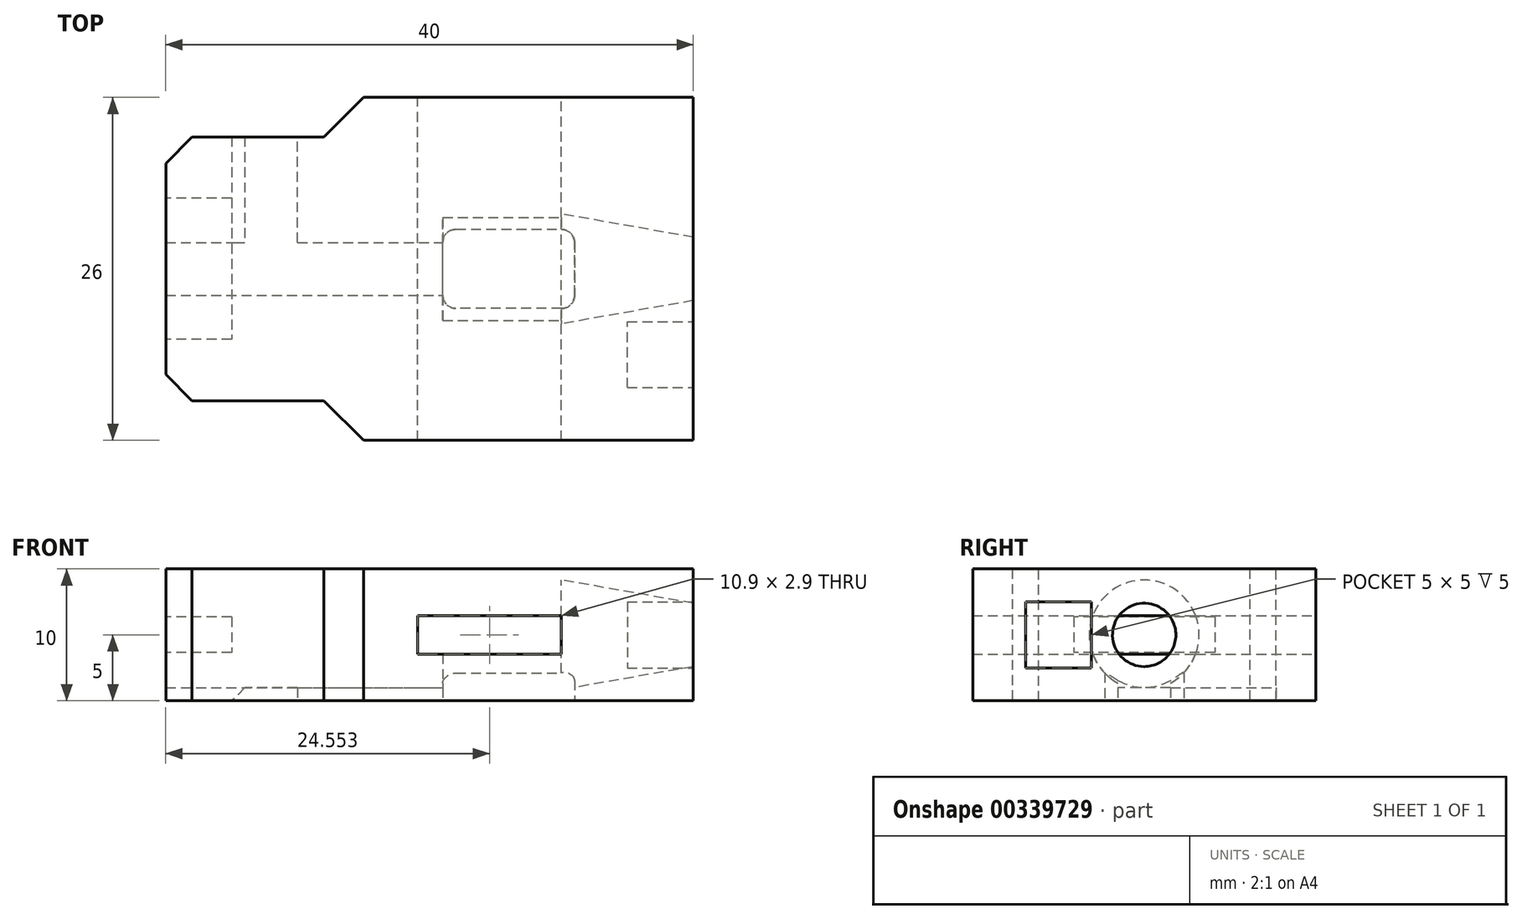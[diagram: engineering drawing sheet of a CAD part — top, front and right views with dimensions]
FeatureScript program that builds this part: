
annotation { "Feature Type Name" : "Feature", "Feature Type Description" : "" }
export const myFeature = defineFeature(function(context is Context, id is Id, definition is map)
    precondition{}
    {
        {
            var Q0;
            Q0=qCreatedBy(makeId("Top.planeOp"),FACE);
            var sketch = newSketch(context, id + "F0", { "sketchPlane" : qUnion([Q0])});
            skPoint(sketch, "E0", {"position": v(-7.73, 0) * mm});
            skLineSegment(sketch, "E1.bottom", {"start": v(-2.73, 10) * mm, "end": v(-12.73, 10) * mm});
            skLineSegment(sketch, "E1.top", {"start": v(-2.73, -10) * mm, "end": v(-12.73, -10) * mm});
            skLineSegment(sketch, "E1.left", {"start": v(-2.73, 10) * mm, "end": v(-2.73, -10) * mm});
            skLineSegment(sketch, "E1.right", {"start": v(-12.73, 10) * mm, "end": v(-12.73, -10) * mm});
            skLineSegment(sketch, "E2", {"start": v(-2.73, 10) * mm, "end": v(-2.73, 13) * mm});
            skLineSegment(sketch, "E3", {"start": v(-2.73, 13) * mm, "end": v(27.27, 13) * mm});
            skLineSegment(sketch, "E4", {"start": v(27.27, 13) * mm, "end": v(27.27, -13) * mm});
            skLineSegment(sketch, "E5", {"start": v(27.27, -13) * mm, "end": v(-2.73, -13) * mm});
            skLineSegment(sketch, "E6", {"start": v(-2.73, -13) * mm, "end": v(-2.73, -10) * mm});
            skSolve(sketch);
        }
        {
            var Q0;
            Q0=makeQuery(id+"F0.imprint","IMPRINT",FACE,{"disambiguationData":[TD([[makeQuery(id+"F0.imprint","IMPRINT",EDGE,{"derivedFrom":sQuery(id+"F0.wireOp",EDGE,"E1.bottom")}),1.0]])]});
            var Q1;
            Q1=makeQuery(id+"F0.imprint","IMPRINT",FACE,{"disambiguationData":[TD([[makeQuery(id+"F0.imprint","IMPRINT",EDGE,{"derivedFrom":sQuery(id+"F0.wireOp",EDGE,"E1.left")}),1.0]])]});
            extrude(context, id + "F1", {"entities" : qUnion([Q0, Q1]), "depth" : 10 * mm});
        }
        {
            var Q0;
            Q0=makeQuery(id+"F1.opExtrude","SWEPT_FACE",FACE,{"disambiguationData":[OSD([sQuery(id+"F0.wireOp",EDGE,"E1.right")])]});
            var sketch = newSketch(context, id + "F2", { "sketchPlane" : qUnion([Q0])});
            skLineSegment(sketch, "E7", {"start": v(-10, 10) * mm, "end": v(10, 0) * mm});
            skLineSegment(sketch, "E8", {"start": v(-10, 0) * mm, "end": v(10, 10) * mm});
            skLineSegment(sketch, "E9.bottom", {"start": v(-5.35, 6.35) * mm, "end": v(5.35, 6.35) * mm});
            skLineSegment(sketch, "E9.top", {"start": v(-5.35, 3.65) * mm, "end": v(5.35, 3.65) * mm});
            skLineSegment(sketch, "E9.left", {"start": v(-5.35, 6.35) * mm, "end": v(-5.35, 3.65) * mm});
            skLineSegment(sketch, "E9.right", {"start": v(5.35, 6.35) * mm, "end": v(5.35, 3.65) * mm});
            skPoint(sketch, "E9.middle", {"position": v(0, 5) * mm});
            skSolve(sketch);
        }
        {
            var Q0;
            {var subQ0=sQuery(id+"F2.wireOp",EDGE,"E9.left");Q0=makeQuery(id+"F2.imprint","IMPRINT",FACE,{"disambiguationData":[TD([[makeQuery(id+"F2.imprint","IMPRINT",EDGE,{"derivedFrom":subQ0}),1.0]])]});}
            var Q1;
            {var subQ0=sQuery(id+"F2.wireOp",EDGE,"E8");var subQ1=sQuery(id+"F2.wireOp",EDGE,"E7");var subQ2=makeQuery(id+"F2.imprint","INTERSECT",VERTEX,{"derivedFrom":[subQ1,subQ0]});Q1=makeQuery(id+"F2.imprint","IMPRINT",FACE,{"disambiguationData":[TD([[makeQuery(id+"F2.imprint","IMPRINT",EDGE,{"disambiguationData":[TD([[subQ2,-1.0]])],"derivedFrom":subQ1}),-1.0]])]});}
            var Q2;
            {var subQ0=sQuery(id+"F2.wireOp",EDGE,"E9.right");Q2=makeQuery(id+"F2.imprint","IMPRINT",FACE,{"disambiguationData":[TD([[makeQuery(id+"F2.imprint","IMPRINT",EDGE,{"derivedFrom":subQ0}),-1.0]])]});}
            var Q3;
            {var subQ0=sQuery(id+"F2.wireOp",EDGE,"E9.bottom");var subQ1=sQuery(id+"F2.wireOp",EDGE,"E7");var subQ2=makeQuery(id+"F2.imprint","INTERSECT",VERTEX,{"derivedFrom":[subQ1,subQ0]});Q3=makeQuery(id+"F2.imprint","IMPRINT",FACE,{"disambiguationData":[TD([[makeQuery(id+"F2.imprint","IMPRINT",EDGE,{"disambiguationData":[TD([[subQ2,-1.0]])],"derivedFrom":subQ1}),1.0]])]});}
            extrude(context, id + "F3", {"entities" : qUnion([Q0, Q1, Q2, Q3]), "operationType" : NewBodyOperationType.REMOVE, "oppositeDirection" : true, "depth" : 5 * mm});
        }
        {
            var Q0;
            Q0=makeQuery(id+"F1.opExtrude","SWEPT_EDGE",EDGE,{"disambiguationData":[OSD([sQuery(id+"F0.wireOp",EDGE,"E2"),sQuery(id+"F0.wireOp",EDGE,"E3")])]});
            var Q1;
            Q1=makeQuery(id+"F1.opExtrude","SWEPT_EDGE",EDGE,{"disambiguationData":[OSD([sQuery(id+"F0.wireOp",EDGE,"E5"),sQuery(id+"F0.wireOp",EDGE,"E6")])]});
            chamfer(context, id + "F4", {"entities" : qUnion([Q0, Q1]), "width" : 5 * mm, "tangentPropagation" : true});
        }
        {
            var Q0;
            Q0=makeQuery(id+"F1.opExtrude","SWEPT_EDGE",EDGE,{"disambiguationData":[OSD([sQuery(id+"F0.wireOp",EDGE,"E1.bottom"),sQuery(id+"F0.wireOp",EDGE,"E1.right")])]});
            var Q1;
            Q1=makeQuery(id+"F1.opExtrude","SWEPT_EDGE",EDGE,{"disambiguationData":[OSD([sQuery(id+"F0.wireOp",EDGE,"E1.top"),sQuery(id+"F0.wireOp",EDGE,"E1.right")])]});
            chamfer(context, id + "F5", {"entities" : qUnion([Q0, Q1]), "width" : 2 * mm, "tangentPropagation" : true});
        }
        {
            var Q0;
            Q0=makeQuery(id+"F1.opExtrude","SWEPT_FACE",FACE,{"disambiguationData":[OSD([sQuery(id+"F0.wireOp",EDGE,"E3")])]});
            var sketch = newSketch(context, id + "F6", { "sketchPlane" : qUnion([Q0])});
            skLineSegment(sketch, "E10", {"start": v(-27.27, 10) * mm, "end": v(-2.27, 0) * mm});
            skLineSegment(sketch, "E11", {"start": v(-2.27, 0) * mm, "end": v(-2.27, 10) * mm});
            skLineSegment(sketch, "E12", {"start": v(-2.27, 10) * mm, "end": v(-27.27, 0) * mm});
            skLineSegment(sketch, "E13", {"start": v(-14.77, 5) * mm, "end": v(-27.27, 5) * mm});
            skLineSegment(sketch, "E14", {"start": v(-14.77, 5) * mm, "end": v(-2.27, 5) * mm});
            skPoint(sketch, "E15", {"position": v(-17.27, 5) * mm});
            skLineSegment(sketch, "E16", {"start": v(-17.27, 5) * mm, "end": v(-17.27, 6.45) * mm});
            skLineSegment(sketch, "E17", {"start": v(-17.27, 6.45) * mm, "end": v(-6.37, 6.45) * mm});
            skLineSegment(sketch, "E18", {"start": v(-6.37, 6.45) * mm, "end": v(-6.37, 5) * mm});
            skLineSegment(sketch, "E19.MirrorCS", {"start": v(-17.27, 3.55) * mm, "end": v(-6.37, 3.55) * mm});
            skLineSegment(sketch, "E20.MirrorCS", {"start": v(-17.27, 5) * mm, "end": v(-17.27, 3.55) * mm});
            skLineSegment(sketch, "E21.MirrorCS", {"start": v(-6.37, 3.55) * mm, "end": v(-6.37, 5) * mm});
            skSolve(sketch);
        }
        {
            var Q0;
            {var subQ5=sQuery(id+"F6.wireOp",EDGE,"E16");Q0=makeQuery(id+"F6.imprint","IMPRINT",FACE,{"disambiguationData":[TD([[makeQuery(id+"F6.imprint","IMPRINT",EDGE,{"derivedFrom":subQ5}),-1.0]])]});}
            var Q1;
            {var subQ3=sQuery(id+"F6.wireOp",EDGE,"E17");var subQ5=sQuery(id+"F6.wireOp",EDGE,"E18");var subQ6=makeQuery(id+"F6.imprint","INTERSECT",VERTEX,{"derivedFrom":[subQ3,subQ5]});Q1=makeQuery(id+"F6.imprint","IMPRINT",FACE,{"disambiguationData":[TD([[makeQuery(id+"F6.imprint","IMPRINT",EDGE,{"disambiguationData":[TD([[subQ6,1.0]])],"derivedFrom":subQ3}),-1.0]])]});}
            var Q2;
            {var subQ5=sQuery(id+"F6.wireOp",EDGE,"E20.MirrorCS");Q2=makeQuery(id+"F6.imprint","IMPRINT",FACE,{"disambiguationData":[TD([[makeQuery(id+"F6.imprint","IMPRINT",EDGE,{"derivedFrom":subQ5}),1.0]])]});}
            var Q3;
            {var subQ3=sQuery(id+"F6.wireOp",EDGE,"E21.MirrorCS");var subQ5=sQuery(id+"F6.wireOp",EDGE,"E19.MirrorCS");var subQ6=makeQuery(id+"F6.imprint","INTERSECT",VERTEX,{"derivedFrom":[subQ5,subQ3]});Q3=makeQuery(id+"F6.imprint","IMPRINT",FACE,{"disambiguationData":[TD([[makeQuery(id+"F6.imprint","IMPRINT",EDGE,{"disambiguationData":[TD([[subQ6,1.0]])],"derivedFrom":subQ5}),1.0]])]});}
            var Q4;
            {var subQ1=sQuery(id+"F6.wireOp",EDGE,"E12");var subQ3=sQuery(id+"F6.wireOp",EDGE,"E18");var subQ4=makeQuery(id+"F6.imprint","INTERSECT",VERTEX,{"derivedFrom":[subQ1,subQ3]});Q4=makeQuery(id+"F6.imprint","IMPRINT",FACE,{"disambiguationData":[TD([[makeQuery(id+"F6.imprint","IMPRINT",EDGE,{"disambiguationData":[TD([[subQ4,-1.0]])],"derivedFrom":subQ3}),-1.0]])]});}
            var Q5;
            {var subQ1=sQuery(id+"F6.wireOp",EDGE,"E10");var subQ3=sQuery(id+"F6.wireOp",EDGE,"E21.MirrorCS");var subQ4=makeQuery(id+"F6.imprint","INTERSECT",VERTEX,{"derivedFrom":[subQ1,subQ3]});Q5=makeQuery(id+"F6.imprint","IMPRINT",FACE,{"disambiguationData":[TD([[makeQuery(id+"F6.imprint","IMPRINT",EDGE,{"disambiguationData":[TD([[subQ4,-1.0]])],"derivedFrom":subQ3}),1.0]])]});}
            var Q6;
            {var subQ1=sQuery(id+"F6.wireOp",EDGE,"E10");var subQ3=sQuery(id+"F6.wireOp",EDGE,"E19.MirrorCS");var subQ4=makeQuery(id+"F6.imprint","INTERSECT",VERTEX,{"derivedFrom":[subQ1,subQ3]});Q6=makeQuery(id+"F6.imprint","IMPRINT",FACE,{"disambiguationData":[TD([[makeQuery(id+"F6.imprint","IMPRINT",EDGE,{"disambiguationData":[TD([[subQ4,1.0]])],"derivedFrom":subQ3}),1.0]])]});}
            var Q7;
            {var subQ1=sQuery(id+"F6.wireOp",EDGE,"E10");var subQ3=sQuery(id+"F6.wireOp",EDGE,"E17");var subQ4=makeQuery(id+"F6.imprint","INTERSECT",VERTEX,{"derivedFrom":[subQ1,subQ3]});Q7=makeQuery(id+"F6.imprint","IMPRINT",FACE,{"disambiguationData":[TD([[makeQuery(id+"F6.imprint","IMPRINT",EDGE,{"disambiguationData":[TD([[subQ4,-1.0]])],"derivedFrom":subQ3}),-1.0]])]});}
            var Q8;
            Q8=makeQuery(id+"F1.opExtrude","SWEPT_FACE",FACE,{"disambiguationData":[OSD([sQuery(id+"F0.wireOp",EDGE,"E5")])]});
            extrude(context, id + "F7", {"entities" : qUnion([Q0, Q1, Q2, Q3, Q4, Q5, Q6, Q7]), "operationType" : NewBodyOperationType.REMOVE, "endBound" : BoundingType.UP_TO_SURFACE, "oppositeDirection" : true, "endBoundEntityFace" : qUnion([Q8]), "depth" : 25 * mm});
        }
        {
            var Q0;
            Q0=makeQuery(id+"F1.opExtrude","SWEPT_FACE",FACE,{"disambiguationData":[OSD([sQuery(id+"F0.wireOp",EDGE,"E4")])]});
            var sketch = newSketch(context, id + "F8", { "sketchPlane" : qUnion([Q0])});
            skLineSegment(sketch, "E22", {"start": v(13, 0) * mm, "end": v(-13, 10) * mm});
            skLineSegment(sketch, "E23", {"start": v(13, 10) * mm, "end": v(-13, 0) * mm});
            skPoint(sketch, "E24", {"position": v(0, 5) * mm});
            skCircle(sketch, "E25", {"center": v(0, 5) * mm, "radius": 2.4 * mm});
            skLineSegment(sketch, "E26", {"start": v(0, 5) * mm, "end": v(-13, 5) * mm});
            skPoint(sketch, "E27", {"position": v(-6.5, 5) * mm});
            skLineSegment(sketch, "E28.bottom", {"start": v(-9, 7.5) * mm, "end": v(-4, 7.5) * mm});
            skLineSegment(sketch, "E28.top", {"start": v(-9, 2.5) * mm, "end": v(-4, 2.5) * mm});
            skLineSegment(sketch, "E28.left", {"start": v(-9, 7.5) * mm, "end": v(-9, 2.5) * mm});
            skLineSegment(sketch, "E28.right", {"start": v(-4, 7.5) * mm, "end": v(-4, 2.5) * mm});
            skSolve(sketch);
        }
        {
            var Q0;
            {var subQ0=sQuery(id+"F8.wireOp",EDGE,"E23");var subQ1=sQuery(id+"F8.wireOp",EDGE,"E22");var subQ2=makeQuery(id+"F8.imprint","INTERSECT",VERTEX,{"derivedFrom":[subQ1,subQ0]});Q0=makeQuery(id+"F8.imprint","IMPRINT",FACE,{"disambiguationData":[TD([[makeQuery(id+"F8.imprint","IMPRINT",EDGE,{"disambiguationData":[TD([[subQ2,-1.0]])],"derivedFrom":subQ1}),1.0]])]});}
            var Q1;
            {var subQ0=sQuery(id+"F8.wireOp",EDGE,"E23");var subQ1=sQuery(id+"F8.wireOp",EDGE,"E22");var subQ2=makeQuery(id+"F8.imprint","INTERSECT",VERTEX,{"derivedFrom":[subQ1,subQ0]});Q1=makeQuery(id+"F8.imprint","IMPRINT",FACE,{"disambiguationData":[TD([[makeQuery(id+"F8.imprint","IMPRINT",EDGE,{"disambiguationData":[TD([[subQ2,-1.0]])],"derivedFrom":subQ1}),-1.0]])]});}
            var Q2;
            {var subQ0=sQuery(id+"F8.wireOp",EDGE,"E25");var subQ1=sQuery(id+"F8.wireOp",EDGE,"E22");var subQ2=makeQuery(id+"F8.imprint","INTERSECT",VERTEX,{"disambiguationData":[OD(0.0)],"derivedFrom":[subQ1,subQ0]});Q2=makeQuery(id+"F8.imprint","IMPRINT",FACE,{"disambiguationData":[TD([[makeQuery(id+"F8.imprint","IMPRINT",EDGE,{"disambiguationData":[TD([[subQ2,-1.0]])],"derivedFrom":subQ1}),-1.0]])]});}
            var Q3;
            {var subQ0=sQuery(id+"F8.wireOp",EDGE,"E25");var subQ1=sQuery(id+"F8.wireOp",EDGE,"E22");var subQ2=makeQuery(id+"F8.imprint","INTERSECT",VERTEX,{"disambiguationData":[OD(0.0)],"derivedFrom":[subQ1,subQ0]});Q3=makeQuery(id+"F8.imprint","IMPRINT",FACE,{"disambiguationData":[TD([[makeQuery(id+"F8.imprint","IMPRINT",EDGE,{"disambiguationData":[TD([[subQ2,-1.0]])],"derivedFrom":subQ1}),1.0]])]});}
            var Q4;
            {var subQ1=sQuery(id+"F8.wireOp",EDGE,"E23");var subQ3=sQuery(id+"F8.wireOp",EDGE,"E25");var subQ4=makeQuery(id+"F8.imprint","INTERSECT",VERTEX,{"disambiguationData":[OD(1.0)],"derivedFrom":[subQ1,subQ3]});Q4=makeQuery(id+"F8.imprint","IMPRINT",FACE,{"disambiguationData":[TD([[makeQuery(id+"F8.imprint","IMPRINT",EDGE,{"disambiguationData":[TD([[subQ4,1.0]])],"derivedFrom":subQ3}),1.0]])]});}
            var Q5;
            Q5=makeQuery(id+"F7.boolean.opBoolean","COPY",FACE,{"derivedFrom":makeQuery(id+"F7.opExtrude","SWEPT_FACE",FACE,{"disambiguationData":[OSD([sQuery(id+"F6.wireOp",EDGE,"E16"),sQuery(id+"F6.wireOp",EDGE,"E20.MirrorCS")])]})});
            extrude(context, id + "F9", {"entities" : qUnion([Q0, Q1, Q2, Q3, Q4]), "operationType" : NewBodyOperationType.REMOVE, "endBound" : BoundingType.UP_TO_SURFACE, "oppositeDirection" : true, "endBoundEntityFace" : qUnion([Q5]), "depth" : 25 * mm, "hasDraft" : true, "draftAngle" : 10 * degree});
        }
        {
            var Q0;
            Q0=makeQuery(id+"F1.opExtrude","CAP_FACE",FACE,{"disambiguationData":[OSD([sQuery(id+"F0.wireOp",EDGE,"E1.bottom"),sQuery(id+"F0.wireOp",EDGE,"E1.top"),sQuery(id+"F0.wireOp",EDGE,"E1.right"),sQuery(id+"F0.wireOp",EDGE,"E2"),sQuery(id+"F0.wireOp",EDGE,"E3"),sQuery(id+"F0.wireOp",EDGE,"E4"),sQuery(id+"F0.wireOp",EDGE,"E5"),sQuery(id+"F0.wireOp",EDGE,"E6")])],"isStart":true});
            var sketch = newSketch(context, id + "F10", { "sketchPlane" : qUnion([Q0])});
            skPoint(sketch, "E29", {"position": v(17.27, 0) * mm});
            skLineSegment(sketch, "E30.bottom", {"start": v(18.27, 3) * mm, "end": v(16.27, 3) * mm});
            skLineSegment(sketch, "E30.top", {"start": v(18.27, -3) * mm, "end": v(16.27, -3) * mm});
            skLineSegment(sketch, "E30.left", {"start": v(18.27, 3) * mm, "end": v(18.27, -3) * mm});
            skLineSegment(sketch, "E31", {"start": v(18.27, 3) * mm, "end": v(8.27, 3) * mm});
            skLineSegment(sketch, "E32", {"start": v(8.27, 3) * mm, "end": v(8.27, -3) * mm});
            skLineSegment(sketch, "E33", {"start": v(8.27, -3) * mm, "end": v(18.27, -3) * mm});
            skSolve(sketch);
        }
        {
            var Q0;
            Q0 = qSketchRegion(id + "F10", true);
            extrude(context, id + "F11", {"entities" : qUnion([Q0]), "operationType" : NewBodyOperationType.REMOVE, "oppositeDirection" : true, "depth" : 5 * mm});
        }
        {
            var Q0;
            {var subQ1=makeQuery(id+"F7.boolean.opBoolean","COPY",FACE,{"derivedFrom":makeQuery(id+"F7.opExtrude","SWEPT_FACE",FACE,{"disambiguationData":[OSD([sQuery(id+"F6.wireOp",EDGE,"E19.MirrorCS")])]})});var subQ2=sQuery(id+"F8.wireOp",EDGE,"E25");Q0=makeQuery(id+"F11.boolean.opBoolean","SPLIT",FACE,{"disambiguationData":[TD([makeQuery(id+"F11.opExtrude","SWEPT_FACE",FACE,{"disambiguationData":[OSD([sQuery(id+"F10.wireOp",EDGE,"E33")])]})])],"derivedFrom":makeQuery(id+"F9.boolean.opBoolean","COPY",FACE,{"disambiguationData":[TD([subQ1])],"derivedFrom":makeQuery(id+"F9.opExtrude","CAP_FACE",FACE,{"disambiguationData":[OSD([subQ2])],"isStart":false})})});}
            var Q1;
            {var subQ1=makeQuery(id+"F7.boolean.opBoolean","COPY",FACE,{"derivedFrom":makeQuery(id+"F7.opExtrude","SWEPT_FACE",FACE,{"disambiguationData":[OSD([sQuery(id+"F6.wireOp",EDGE,"E19.MirrorCS")])]})});var subQ2=sQuery(id+"F8.wireOp",EDGE,"E25");Q1=makeQuery(id+"F11.boolean.opBoolean","SPLIT",FACE,{"disambiguationData":[TD([makeQuery(id+"F11.opExtrude","SWEPT_FACE",FACE,{"disambiguationData":[OSD([sQuery(id+"F10.wireOp",EDGE,"E31")])]})])],"derivedFrom":makeQuery(id+"F9.boolean.opBoolean","COPY",FACE,{"disambiguationData":[TD([subQ1])],"derivedFrom":makeQuery(id+"F9.opExtrude","CAP_FACE",FACE,{"disambiguationData":[OSD([subQ2])],"isStart":false})})});}
            var Q2;
            Q2=makeQuery(id+"F11.boolean.opBoolean","COPY",FACE,{"derivedFrom":makeQuery(id+"F11.opExtrude","SWEPT_FACE",FACE,{"disambiguationData":[OSD([sQuery(id+"F10.wireOp",EDGE,"E32")])]})});
            extrude(context, id + "F12", {"entities" : qUnion([Q0, Q1]), "operationType" : NewBodyOperationType.REMOVE, "endBound" : BoundingType.UP_TO_SURFACE, "oppositeDirection" : true, "endBoundEntityFace" : qUnion([Q2]), "depth" : 4.47 * mm});
        }
        {
            var Q0;
            Q0=makeQuery(id+"F11.boolean.opBoolean","COPY",EDGE,{"derivedFrom":makeQuery(id+"F11.opExtrude","SWEPT_EDGE",EDGE,{"disambiguationData":[OSD([sQuery(id+"F10.wireOp",EDGE,"E30.left"),sQuery(id+"F10.wireOp",EDGE,"E31")])]})});
            var Q1;
            Q1=makeQuery(id+"F11.boolean.opBoolean","COPY",EDGE,{"derivedFrom":makeQuery(id+"F11.opExtrude","SWEPT_EDGE",EDGE,{"disambiguationData":[OSD([sQuery(id+"F10.wireOp",EDGE,"E31"),sQuery(id+"F10.wireOp",EDGE,"E32")])]})});
            var Q2;
            Q2=makeQuery(id+"F11.boolean.opBoolean","COPY",EDGE,{"derivedFrom":makeQuery(id+"F11.opExtrude","SWEPT_EDGE",EDGE,{"disambiguationData":[OSD([sQuery(id+"F10.wireOp",EDGE,"E32"),sQuery(id+"F10.wireOp",EDGE,"E33")])]})});
            var Q3;
            Q3=makeQuery(id+"F11.boolean.opBoolean","COPY",EDGE,{"derivedFrom":makeQuery(id+"F11.opExtrude","SWEPT_EDGE",EDGE,{"disambiguationData":[OSD([sQuery(id+"F10.wireOp",EDGE,"E30.left"),sQuery(id+"F10.wireOp",EDGE,"E33")])]})});
            fillet(context, id + "F13", {"entities" : qUnion([Q0, Q1, Q2, Q3]), "radius" : 1 * mm, "tangentPropagation" : true, "allowEdgeOverflow" : false});
        }
        {
            var Q0;
            Q0=makeQuery(id+"F1.opExtrude","CAP_FACE",FACE,{"disambiguationData":[OSD([sQuery(id+"F0.wireOp",EDGE,"E1.bottom"),sQuery(id+"F0.wireOp",EDGE,"E1.top"),sQuery(id+"F0.wireOp",EDGE,"E1.right"),sQuery(id+"F0.wireOp",EDGE,"E2"),sQuery(id+"F0.wireOp",EDGE,"E3"),sQuery(id+"F0.wireOp",EDGE,"E4"),sQuery(id+"F0.wireOp",EDGE,"E5"),sQuery(id+"F0.wireOp",EDGE,"E6")])],"isStart":true});
            var sketch = newSketch(context, id + "F14", { "sketchPlane" : qUnion([Q0])});
            skLineSegment(sketch, "E34.bottom", {"start": v(-12.73, 2) * mm, "end": v(18.27, 2) * mm});
            skLineSegment(sketch, "E34.top", {"start": v(-12.73, -2) * mm, "end": v(18.27, -2) * mm});
            skLineSegment(sketch, "E34.left", {"start": v(-12.73, 2) * mm, "end": v(-12.73, -2) * mm});
            skLineSegment(sketch, "E34.right", {"start": v(18.27, 2) * mm, "end": v(18.27, -2) * mm});
            skLineSegment(sketch, "E35.bottom", {"start": v(-12.73, -2) * mm, "end": v(-2.73, -2) * mm});
            skLineSegment(sketch, "E35.top", {"start": v(-6.73, -10) * mm, "end": v(-2.73, -10) * mm});
            skLineSegment(sketch, "E35.right", {"start": v(-2.73, -2) * mm, "end": v(-2.73, -10) * mm});
            skLineSegment(sketch, "E36", {"start": v(-6.73, -10) * mm, "end": v(-6.73, -2) * mm});
            skSolve(sketch);
        }
        {
            var Q0;
            {var subQ1=sQuery(id+"F14.wireOp",EDGE,"E34.left");Q0=makeQuery(id+"F14.imprint","IMPRINT",FACE,{"disambiguationData":[TD([[makeQuery(id+"F14.imprint","IMPRINT",EDGE,{"derivedFrom":subQ1}),-1.0]])]});}
            var Q1;
            Q1=makeQuery(id+"F14.imprint","IMPRINT",FACE,{"disambiguationData":[TD([[makeQuery(id+"F14.imprint","IMPRINT",EDGE,{"derivedFrom":sQuery(id+"F14.wireOp",EDGE,"E35.top")}),-1.0]])]});
            extrude(context, id + "F15", {"entities" : qUnion([Q0, Q1]), "operationType" : NewBodyOperationType.REMOVE, "oppositeDirection" : true, "depth" : 1 * mm});
        }
        {
            var Q0;
            Q0=makeQuery(id+"F15.boolean.opBoolean","COPY",EDGE,{"derivedFrom":makeQuery(id+"F15.opExtrude","CAP_EDGE",EDGE,{"disambiguationData":[OSD([sQuery(id+"F14.wireOp",EDGE,"E36")])],"isStart":true})});
            chamfer(context, id + "F16", {"entities" : qUnion([Q0]), "width" : 1 * mm, "tangentPropagation" : true});
        }
        {
            var Q0;
            {var subQ0=sQuery(id+"F8.wireOp",EDGE,"E28.right");var subQ1=sQuery(id+"F8.wireOp",EDGE,"E22");var subQ2=makeQuery(id+"F8.imprint","INTERSECT",VERTEX,{"derivedFrom":[subQ1,subQ0]});Q0=makeQuery(id+"F8.imprint","IMPRINT",FACE,{"disambiguationData":[TD([[makeQuery(id+"F8.imprint","IMPRINT",EDGE,{"disambiguationData":[TD([[subQ2,-1.0]])],"derivedFrom":subQ1}),-1.0]])]});}
            var Q1;
            {var subQ5=sQuery(id+"F8.wireOp",EDGE,"E22");var subQ7=sQuery(id+"F8.wireOp",EDGE,"E28.right");var subQ9=makeQuery(id+"F8.imprint","INTERSECT",VERTEX,{"derivedFrom":[subQ5,subQ7]});Q1=makeQuery(id+"F8.imprint","IMPRINT",FACE,{"disambiguationData":[TD([[makeQuery(id+"F8.imprint","IMPRINT",EDGE,{"disambiguationData":[TD([[subQ9,-1.0]])],"derivedFrom":subQ5}),1.0]])]});}
            var Q2;
            {var subQ5=sQuery(id+"F8.wireOp",EDGE,"E23");var subQ7=sQuery(id+"F8.wireOp",EDGE,"E28.right");var subQ9=makeQuery(id+"F8.imprint","INTERSECT",VERTEX,{"derivedFrom":[subQ5,subQ7]});Q2=makeQuery(id+"F8.imprint","IMPRINT",FACE,{"disambiguationData":[TD([[makeQuery(id+"F8.imprint","IMPRINT",EDGE,{"disambiguationData":[TD([[subQ9,-1.0]])],"derivedFrom":subQ5}),-1.0]])]});}
            var Q3;
            {var subQ0=sQuery(id+"F8.wireOp",EDGE,"E28.right");var subQ1=sQuery(id+"F8.wireOp",EDGE,"E23");var subQ2=makeQuery(id+"F8.imprint","INTERSECT",VERTEX,{"derivedFrom":[subQ1,subQ0]});Q3=makeQuery(id+"F8.imprint","IMPRINT",FACE,{"disambiguationData":[TD([[makeQuery(id+"F8.imprint","IMPRINT",EDGE,{"disambiguationData":[TD([[subQ2,-1.0]])],"derivedFrom":subQ1}),1.0]])]});}
            extrude(context, id + "F17", {"entities" : qUnion([Q0, Q1, Q2, Q3]), "operationType" : NewBodyOperationType.REMOVE, "oppositeDirection" : true, "depth" : 5 * mm});
        }
    });
